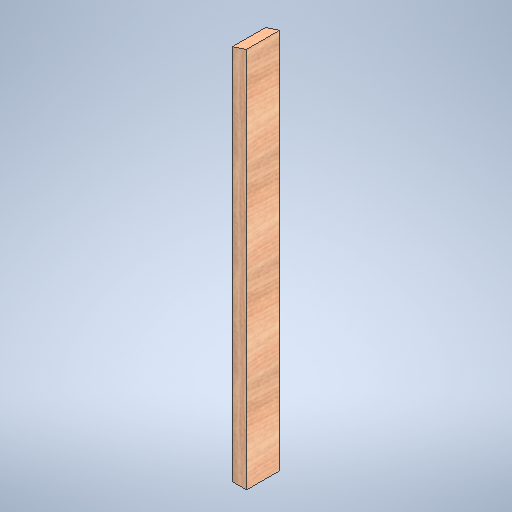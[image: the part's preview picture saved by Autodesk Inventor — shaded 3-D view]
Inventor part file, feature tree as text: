
AUTODESK INVENTOR PART (.ipt)
format: ipt  version: 2025.1 (Build 291241020, 241B)  size: 317,952 bytes
history: native  units: in
note: dims shown in document units (in); Inventor stores cm internally (conversion verified against a paired STEP export)
features: extrude x1, sketch x1
ambient origin geometry x8: Origin, YZ Plane, XZ Plane, XY Plane, X Axis, Y Axis, Z Axis, Center Point
bodies: Solid1 (feature_tree)
feature tree (2):
  extrude  "Extrusion1"  Depth=3.5in TaperAngle=0.0deg
  sketch  "Sketch1"  dims[d2=1.5in d3=3.5in d4=0.0in d5=39.873in d6=40.373in]
